# Revit family: SIM_ELE_MASK
name_source: partatom
category: Electrical Equipment
units: mm (PartAtom-declared; Revit-internal decimal feet)

## family parameters
Always vertical = Yes
Cut with Voids When Loaded = No
Maintain Annotation Orientation = No
OmniClass Number = 23.80.30.11.17
OmniClass Title = Distribution Boards and Control Panels
Panel Configuration = Two Columns, Circuits Across
Part Type = Panelboard
Room Calculation Point = No
Round Connector Dimension = Use Diameter
Shared = No
Work Plane-Based = No

## types (1)
- SIM_ELE_MASK
    Default Elevation = 0 mm  [stored 0 ft]
    Height = 6200 mm  [stored 20.3412 ft]
    Hexagonal nut S1 = 30 mm
    Washer Radius1 = 18 mm
    Washer Raduis2 = 35 mm
    r1 = 15 mm
    r2 = 34 mm
    r3 = 15 mm

note: [stored X ft] marks values corroborated as IEEE doubles in the binary element streams (Revit-internal decimal feet)

## geometry (parser evidence)
native form markers: Sweep x4
no freeform markers — native parametric forms only
